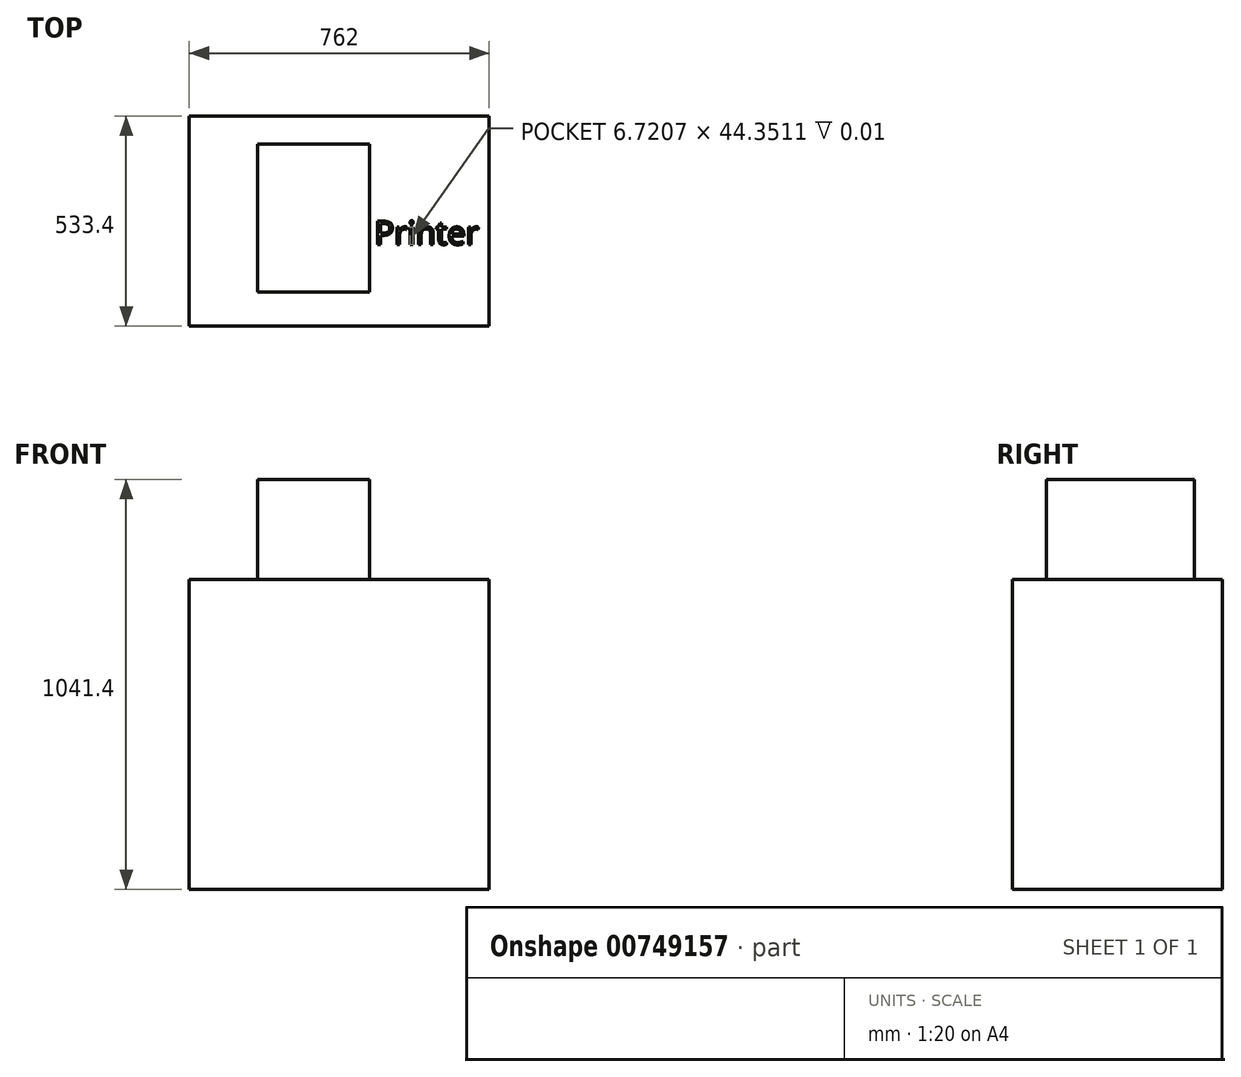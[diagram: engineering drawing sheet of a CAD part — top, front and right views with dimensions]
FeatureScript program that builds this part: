
annotation { "Feature Type Name" : "Feature", "Feature Type Description" : "" }
export const myFeature = defineFeature(function(context is Context, id is Id, definition is map)
    precondition{}
    {
        {
            var Q0;
            Q0=qCreatedBy(makeId("Top.planeOp"),FACE);
            var sketch = newSketch(context, id + "F0", { "sketchPlane" : qUnion([Q0])});
            skLineSegment(sketch, "E0.bottom", {"start": v(0, 0) * mm, "end": v(762, 0) * mm});
            skLineSegment(sketch, "E0.top", {"start": v(0, 533.4) * mm, "end": v(762, 533.4) * mm});
            skLineSegment(sketch, "E0.left", {"start": v(0, 0) * mm, "end": v(0, 533.4) * mm});
            skLineSegment(sketch, "E0.right", {"start": v(762, 0) * mm, "end": v(762, 533.4) * mm});
            skSolve(sketch);
        }
        {
            var Q0;
            Q0 = qSketchRegion(id + "F0", true);
            extrude(context, id + "F1", {"entities" : qUnion([Q0]), "depth" : 787.4 * mm, "offsetDistance" : 25.4 * mm});
        }
        {
            var Q0;
            Q0=makeQuery(id+"F1.opExtrude","CAP_FACE",FACE,{"disambiguationData":[OSD([sQuery(id+"F0.wireOp",EDGE,"E0.bottom"),sQuery(id+"F0.wireOp",EDGE,"E0.top"),sQuery(id+"F0.wireOp",EDGE,"E0.left"),sQuery(id+"F0.wireOp",EDGE,"E0.right")])],"isStart":false});
            var sketch = newSketch(context, id + "F2", { "sketchPlane" : qUnion([Q0])});
            skLineSegment(sketch, "E1.bottom", {"start": v(173.92, 462.65) * mm, "end": v(458.54, 462.65) * mm});
            skLineSegment(sketch, "E1.top", {"start": v(173.92, 86.41) * mm, "end": v(458.54, 86.41) * mm});
            skLineSegment(sketch, "E1.left", {"start": v(173.92, 462.65) * mm, "end": v(173.92, 86.41) * mm});
            skLineSegment(sketch, "E1.right", {"start": v(458.54, 462.65) * mm, "end": v(458.54, 86.41) * mm});
            skSolve(sketch);
        }
        {
            var Q0;
            Q0 = qSketchRegion(id + "F2", true);
            extrude(context, id + "F3", {"entities" : qUnion([Q0]), "operationType" : NewBodyOperationType.ADD, "depth" : 254 * mm, "offsetDistance" : 25.4 * mm});
        }
        {
            var Q0;
            Q0=makeQuery(id+"F1.opExtrude","CAP_FACE",FACE,{"disambiguationData":[OSD([sQuery(id+"F0.wireOp",EDGE,"E0.bottom"),sQuery(id+"F0.wireOp",EDGE,"E0.top"),sQuery(id+"F0.wireOp",EDGE,"E0.left"),sQuery(id+"F0.wireOp",EDGE,"E0.right")])],"isStart":false});
            var sketch = newSketch(context, id + "F4", { "sketchPlane" : qUnion([Q0])});
            skText(sketch, "E2", { "text": "Printer", "fontName": "OpenSans-Regular.ttf"});
            skPoint(sketch, "E3", {"position": v(762, 266.7) * mm});
            const initialGuessF4  = {"E2": [0.47073, 0.20703, 1, 0, 0.05967]};
            skSetInitialGuess(sketch, initialGuessF4);
            skSolve(sketch);
        }
        {
            var Q0;
            Q0 = qSketchRegion(id + "F4", true);
            extrude(context, id + "F5", {"entities" : qUnion([Q0]), "operationType" : NewBodyOperationType.REMOVE, "oppositeDirection" : true, "depth" : 1 / 101.6 * mm, "offsetDistance" : 25.4 * mm});
        }
    });
